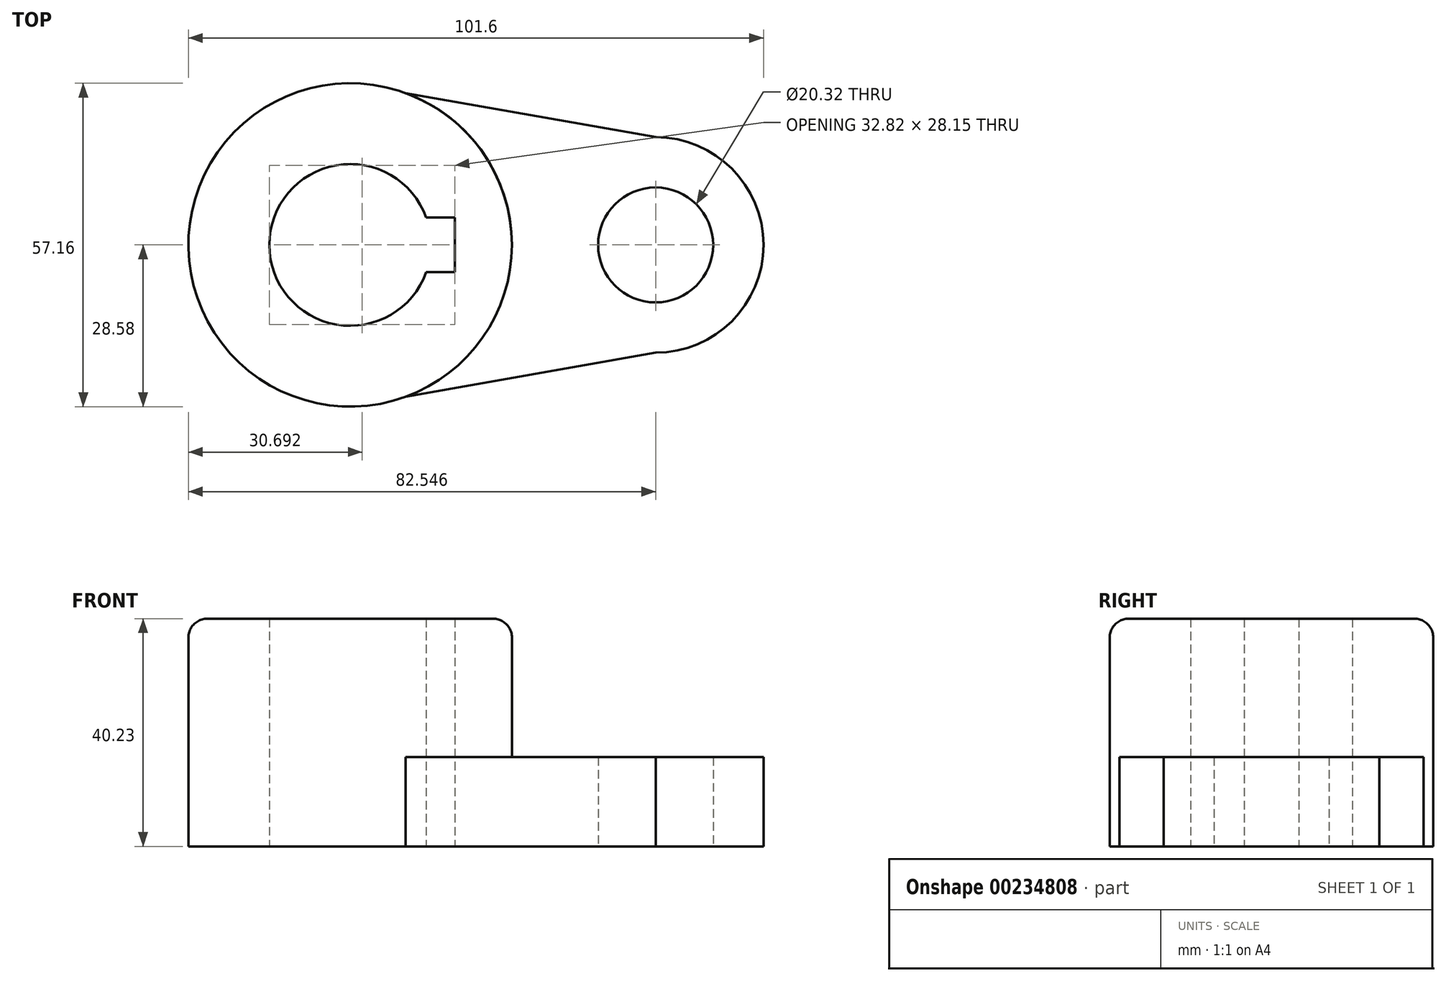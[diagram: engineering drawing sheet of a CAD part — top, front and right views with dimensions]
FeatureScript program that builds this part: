
annotation { "Feature Type Name" : "Feature", "Feature Type Description" : "" }
export const myFeature = defineFeature(function(context is Context, id is Id, definition is map)
    precondition{}
    {
        {
            var Q0;
            Q0=qCreatedBy(makeId("Top.planeOp"),FACE);
            var sketch = newSketch(context, id + "F0", { "sketchPlane" : qUnion([Q0])});
            skCircle(sketch, "E0", {"center": v(-26.84, 0) * mm, "radius": 28.57 * mm});
            skArc(sketch, "E1", {"start": v(-13.4, 4.83) * mm, "mid": v(-41.13, 0) * mm, "end": v(-13.4, -4.83) * mm});
            skArc(sketch, "E2", {"start": v(27.14, -19.05) * mm, "mid": v(46.19, 0) * mm, "end": v(27.14, 19.05) * mm});
            skCircle(sketch, "E3", {"center": v(27.14, 0) * mm, "radius": 10.16 * mm});
            skLineSegment(sketch, "E4", {"start": v(27.14, 19.05) * mm, "end": v(-17.06, 26.85) * mm});
            skLineSegment(sketch, "E5", {"start": v(-17.06, -26.85) * mm, "end": v(27.14, -19.05) * mm});
            skLineSegment(sketch, "E6.bottom", {"start": v(-8.3, 4.83) * mm, "end": v(-13.4, 4.83) * mm});
            skLineSegment(sketch, "E6.top", {"start": v(-8.3, -4.83) * mm, "end": v(-13.4, -4.83) * mm});
            skLineSegment(sketch, "E6.left", {"start": v(-8.3, 4.83) * mm, "end": v(-8.3, -4.83) * mm});
            skSolve(sketch);
        }
        {
            var Q0;
            Q0=makeQuery(id+"F0.imprint","IMPRINT",FACE,{"disambiguationData":[TD([[makeQuery(id+"F0.imprint","IMPRINT",EDGE,{"derivedFrom":sQuery(id+"F0.wireOp",EDGE,"E1")}),-1.0]])]});
            extrude(context, id + "F1", {"entities" : qUnion([Q0]), "depth" : 40.23 * mm});
        }
        {
            var Q0;
            Q0=makeQuery(id+"F0.imprint","IMPRINT",FACE,{"disambiguationData":[TD([[makeQuery(id+"F0.imprint","IMPRINT",EDGE,{"derivedFrom":sQuery(id+"F0.wireOp",EDGE,"E2")}),1.0]])]});
            extrude(context, id + "F2", {"entities" : qUnion([Q0]), "operationType" : NewBodyOperationType.ADD, "depth" : 15.77 * mm});
        }
        {
            var Q0;
            Q0=makeQuery(id+"F1.opExtrude","CAP_EDGE",EDGE,{"disambiguationData":[OSD([sQuery(id+"F0.wireOp",EDGE,"E0")])],"isStart":false});
            fillet(context, id + "F3", {"entities" : qUnion([Q0]), "radius" : 3.3 * mm, "tangentPropagation" : true, "allowEdgeOverflow" : false});
        }
    });
